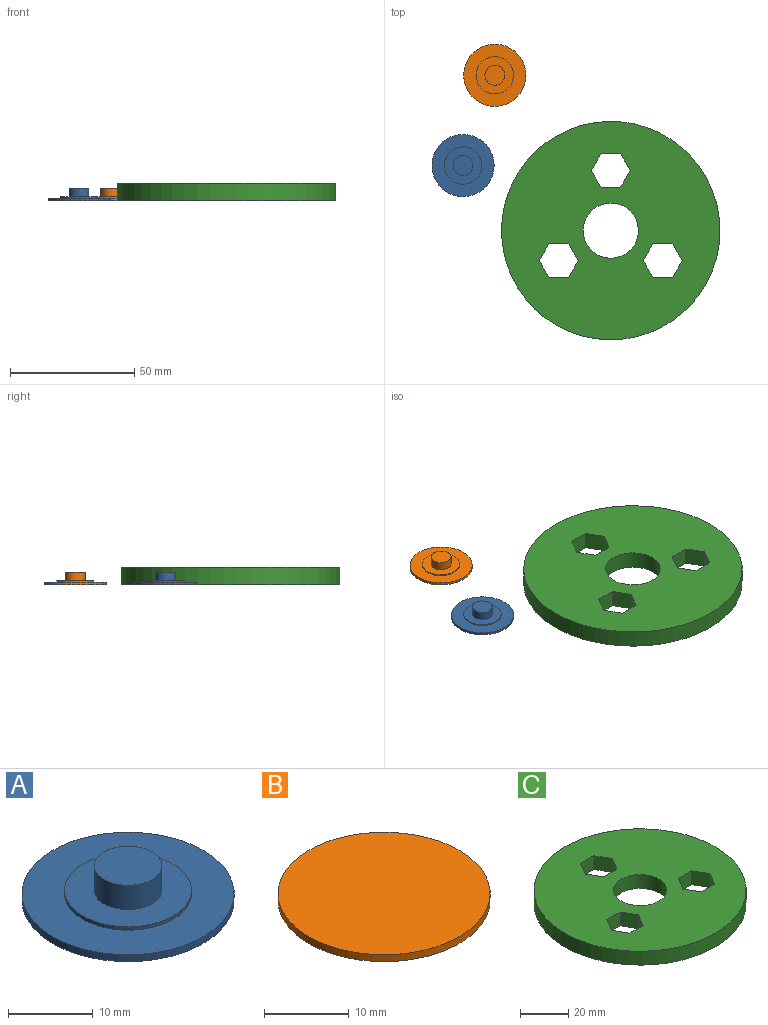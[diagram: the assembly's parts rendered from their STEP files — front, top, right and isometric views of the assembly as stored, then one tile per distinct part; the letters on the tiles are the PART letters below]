
ASSEMBLY  parts=3 mates=2
PART A: 124 faces, bbox 25x25x5 mm
  f0: plane 25x25mm, normal (0,0,-1), area 410mm2, adj f6,f7,f8,f9,f12,f20,f21,f22
  f1: cylinder r=4mm len=8mm, axis (0,0,1), area 88mm2, adj f2,f3
  f2: plane 8x8mm, normal (0,0,1), area 50.3mm2, adj f1
  f3: plane 15x15mm, normal (0,0,1), area 126.4mm2, adj f1,f4
  f4: cylinder r=7.5mm len=15mm, axis (0,0,1), area 23.6mm2, adj f3,f5
  f5: plane 25x25mm, normal (0,0,1), area 314.2mm2, adj f4,f6
  f6: cylinder r=12.5mm len=25mm, axis (0,0,1), area 78.5mm2, adj f0,f5
  f7: extruded ~0.28x0.25mm, area 0.1mm2, adj f0,f8,f12,f13
  f8: cylinder r=3.22mm len=6.45mm, axis (0,0,-1), area 4.7mm2, adj f0,f7,f9,f13
  f9: extruded ~0.29x0.25mm, area 0.1mm2, adj f0,f8,f12,f13
  f10: cylinder r=2.57mm len=5.14mm, axis (0,0,-1), area 4mm2, adj f13,f17
  f11: cylinder r=2.62mm len=5.24mm, axis (0,0,-1), area 4.1mm2, adj f13,f14
  f12: cylinder r=3.28mm len=6.56mm, axis (0,0,-1), area 4.8mm2, adj f0,f7,f9,f13
  f13: plane 13x6.64mm, normal (0,0,-1), area 24.1mm2, adj f7,f8,f9,f10,f11,f12
  f14: plane 5.24x5.24mm, normal (0,0,-1), area 9mm2, adj f11,f15
  f15: cylinder r=2mm len=3.99mm, axis (0,0,-1), area 3.1mm2, adj f14,f16
  f16: plane 3.99x3.99mm, normal (0,0,-1), area 12.5mm2, adj f15
  f17: plane 5.14x5.14mm, normal (0,0,-1), area 9.4mm2, adj f10,f18
  f18: cylinder r=1.9mm len=3.8mm, axis (0,0,-1), area 3mm2, adj f17,f19
  f19: plane 3.8x3.8mm, normal (0,0,-1), area 11.4mm2, adj f18
  f20: extruded ~0.25x0.21mm, area 0.1mm2, adj f0,f21,f35,f36
  f21: extruded ~0.27x0.25mm, area 0.1mm2, adj f0,f20,f22,f36
  f22: extruded ~0.31x0.25mm, area 0.1mm2, adj f0,f21,f23,f36
  f23: extruded ~0.31x0.25mm, area 0.1mm2, adj f0,f22,f24,f36
  f24: extruded ~0.56x0.25mm, area 0.2mm2, adj f0,f23,f25,f36
  f25: plane 0.34x0.25mm, normal (-1,0,0), area 0.1mm2, adj f0,f24,f26,f36
  f26: extruded ~0.27x0.25mm, area 0.1mm2, adj f0,f25,f27,f36
  f27: extruded ~0.27x0.25mm, area 0.1mm2, adj f0,f26,f28,f36
  f28: extruded ~0.25x0.22mm, area 0.1mm2, adj f0,f27,f29,f36
  f29: extruded ~0.26x0.25mm, area 0.1mm2, adj f0,f28,f30,f36
  f30: extruded ~0.33x0.25mm, area 0.1mm2, adj f0,f29,f31,f36
  f31: extruded ~0.28x0.25mm, area 0.1mm2, adj f0,f30,f32,f36
  f32: extruded ~0.56x0.25mm, area 0.2mm2, adj f0,f31,f33,f36
  f33: plane 0.35x0.25mm, normal (1,0,0), area 0.1mm2, adj f0,f32,f34,f36
  f34: extruded ~0.27x0.25mm, area 0.1mm2, adj f0,f33,f35,f36
  f35: extruded ~0.27x0.25mm, area 0.1mm2, adj f0,f20,f34,f36
  f36: plane 2.2x0.6mm, normal (0,0,-1), area 0.7mm2, adj f20,f21,f22,f23,f24,f25,f26,f27
  f37: plane 3.56x0.25mm, normal (-1,0,0), area 0.9mm2, adj f0,f38,f40,f41
  f38: plane 0.38x0.25mm, normal (0,1,0), area 0.1mm2, adj f0,f37,f39,f41
  f39: plane 3.56x0.25mm, normal (1,0,0), area 0.9mm2, adj f0,f38,f40,f41
  f40: plane 0.38x0.25mm, normal (0,-1,0), area 0.1mm2, adj f0,f37,f39,f41
  f41: plane 3.56x0.38mm, normal (0,0,-1), area 1.4mm2, adj f37,f38,f39,f40
  f42: plane 1.28x0.92mm, normal (0.81,0.58,0), area 0.4mm2, adj f0,f43,f53,f54
  f43: plane 0.43x0.25mm, normal (0,-1,0), area 0.1mm2, adj f0,f42,f44,f54
  f44: plane 1.02x0.71mm, normal (-0.82,-0.57,0), area 0.3mm2, adj f0,f43,f45,f54
  f45: plane 1.02x0.7mm, normal (0.82,-0.57,0), area 0.3mm2, adj f0,f44,f46,f54
  f46: plane 0.43x0.25mm, normal (0,-1,0), area 0.1mm2, adj f0,f45,f47,f54
  f47: plane 1.28x0.92mm, normal (-0.81,0.58,0), area 0.4mm2, adj f0,f46,f48,f54
  f48: plane 1.22x0.87mm, normal (-0.81,-0.58,0), area 0.4mm2, adj f0,f47,f49,f54
  f49: plane 0.43x0.25mm, normal (0,1,0), area 0.1mm2, adj f0,f48,f50,f54
  f50: plane 0.96x0.66mm, normal (0.82,0.57,0), area 0.3mm2, adj f0,f49,f51,f54
  f51: plane 0.96x0.66mm, normal (-0.82,0.57,0), area 0.3mm2, adj f0,f50,f52,f54
  f52: plane 0.43x0.25mm, normal (0,1,0), area 0.1mm2, adj f0,f51,f53,f54
  f53: plane 1.22x0.87mm, normal (0.81,-0.58,0), area 0.4mm2, adj f0,f42,f52,f54
  f54: plane 2.51x2.27mm, normal (0,0,-1), area 2mm2, adj f42,f43,f44,f45,f46,f47,f48,f49
  f55: extruded ~0.25x0.21mm, area 0.1mm2, adj f0,f56,f70,f71
  f56: extruded ~0.27x0.25mm, area 0.1mm2, adj f0,f55,f57,f71
  f57: extruded ~0.31x0.25mm, area 0.1mm2, adj f0,f56,f58,f71
  f58: extruded ~0.31x0.25mm, area 0.1mm2, adj f0,f57,f59,f71
  f59: extruded ~0.56x0.25mm, area 0.2mm2, adj f0,f58,f60,f71
  f60: plane 0.34x0.25mm, normal (-1,0,0), area 0.1mm2, adj f0,f59,f61,f71
  f61: extruded ~0.27x0.25mm, area 0.1mm2, adj f0,f60,f62,f71
  f62: extruded ~0.27x0.25mm, area 0.1mm2, adj f0,f61,f63,f71
  f63: extruded ~0.25x0.22mm, area 0.1mm2, adj f0,f62,f64,f71
  f64: extruded ~0.26x0.25mm, area 0.1mm2, adj f0,f63,f65,f71
  f65: extruded ~0.33x0.25mm, area 0.1mm2, adj f0,f64,f66,f71
  f66: extruded ~0.28x0.25mm, area 0.1mm2, adj f0,f65,f67,f71
  f67: extruded ~0.56x0.25mm, area 0.2mm2, adj f0,f66,f68,f71
  f68: plane 0.35x0.25mm, normal (1,0,0), area 0.1mm2, adj f0,f67,f69,f71
  f69: extruded ~0.27x0.25mm, area 0.1mm2, adj f0,f68,f70,f71
  f70: extruded ~0.27x0.25mm, area 0.1mm2, adj f0,f55,f69,f71
  f71: plane 2.2x0.6mm, normal (0,0,-1), area 0.7mm2, adj f55,f56,f57,f58,f59,f60,f61,f62
  f72: extruded ~0.43x0.25mm, area 0.1mm2, adj f0,f73,f90,f91
  f73: extruded ~0.38x0.25mm, area 0.1mm2, adj f0,f72,f74,f91
  f74: plane 0.34x0.25mm, normal (-1,0,0), area 0.1mm2, adj f0,f73,f75,f91
  f75: extruded ~0.8x0.25mm, area 0.2mm2, adj f0,f74,f76,f91
  f76: extruded ~0.6x0.25mm, area 0.2mm2, adj f0,f75,f77,f91
  f77: extruded ~0.67x0.25mm, area 0.2mm2, adj f0,f76,f78,f91
  f78: plane 1.73x0.25mm, normal (0,-1,0), area 0.4mm2, adj f0,f77,f79,f91
  f79: plane 0.25x0.24mm, normal (-1,0,0), area 0.1mm2, adj f0,f78,f80,f91
  f80: extruded ~0.82x0.27mm, area 0.2mm2, adj f0,f79,f81,f91
  f81: extruded ~0.75x0.31mm, area 0.2mm2, adj f0,f80,f82,f91
  f82: extruded ~0.8x0.36mm, area 0.2mm2, adj f0,f81,f83,f91
  f83: extruded ~0.96x0.3mm, area 0.3mm2, adj f0,f82,f84,f91
  f84: extruded ~0.94x0.32mm, area 0.3mm2, adj f0,f83,f90,f91
  f85: extruded ~0.46x0.25mm, area 0.1mm2, adj f86,f89,f91,f92
  f86: extruded ~0.55x0.25mm, area 0.1mm2, adj f85,f87,f91,f92
  f87: plane 1.31x0.25mm, normal (0,1,0), area 0.3mm2, adj f86,f88,f91,f92
  f88: extruded ~0.54x0.25mm, area 0.1mm2, adj f87,f89,f91,f92
  f89: extruded ~0.48x0.25mm, area 0.1mm2, adj f85,f88,f91,f92
  f90: extruded ~0.88x0.34mm, area 0.2mm2, adj f0,f72,f84,f91
  f91: plane 2.6x2.12mm, normal (0,0,-1), area 2.5mm2, adj f72,f73,f74,f75,f76,f77,f78,f79
  f92: plane 1.31x0.74mm, normal (0,0,-1), area 0.8mm2, adj f85,f86,f87,f88,f89
  f93: plane 0.4x0.25mm, normal (0,-1,0), area 0.1mm2, adj f0,f94,f105,f106
  f94: plane 3.36x1.32mm, normal (-0.93,0.36,0), area 0.9mm2, adj f0,f93,f95,f106
  f95: plane 0.33x0.25mm, normal (0,1,0), area 0.1mm2, adj f0,f94,f96,f106
  f96: plane 3.36x1.32mm, normal (0.93,0.37,0), area 0.9mm2, adj f0,f95,f97,f106
  f97: plane 0.39x0.25mm, normal (0,-1,0), area 0.1mm2, adj f0,f96,f98,f106
  f98: plane 1.06x0.41mm, normal (-0.93,-0.36,0), area 0.3mm2, adj f0,f97,f99,f106
  f99: plane 1.34x0.25mm, normal (0,-1,0), area 0.3mm2, adj f0,f98,f105,f106
  f100: plane 1.08x0.25mm, normal (0,1,0), area 0.3mm2, adj f101,f104,f106,f107
  f101: plane 1.04x0.39mm, normal (-0.94,-0.35,0), area 0.3mm2, adj f100,f102,f106,f107
  f102: extruded ~0.48x0.25mm, area 0.1mm2, adj f101,f103,f106,f107
  f103: extruded ~0.48x0.25mm, area 0.1mm2, adj f102,f104,f106,f107
  f104: plane 1.04x0.39mm, normal (0.94,-0.35,0), area 0.3mm2, adj f100,f103,f106,f107
  f105: plane 1.06x0.42mm, normal (0.93,-0.36,0), area 0.3mm2, adj f0,f93,f99,f106
  f106: plane 3.36x2.96mm, normal (0,0,-1), area 2.9mm2, adj f93,f94,f95,f96,f97,f98,f99,f100
  f107: plane 1.52x1.08mm, normal (0,0,-1), area 0.8mm2, adj f100,f101,f102,f103,f104
  f108: plane 0.35x0.25mm, normal (1,0,0), area 0.1mm2, adj f0,f109,f114,f115
  f109: plane 2.2x0.97mm, normal (-0.4,-0.92,0), area 0.6mm2, adj f0,f108,f110,f115
  f110: plane 0.25x0.22mm, normal (-1,0,0), area 0.1mm2, adj f0,f109,f111,f115
  f111: plane 2.2x1.1mm, normal (-0.45,0.89,0), area 0.6mm2, adj f0,f110,f112,f115
  f112: plane 0.34x0.25mm, normal (1,0,0), area 0.1mm2, adj f0,f111,f113,f115
  f113: plane 1.79x0.85mm, normal (0.43,-0.9,0), area 0.5mm2, adj f0,f112,f114,f115
  f114: plane 1.79x0.75mm, normal (0.38,0.92,0), area 0.5mm2, adj f0,f108,f113,f115
  f115: plane 2.28x2.2mm, normal (0,0,-1), area 1.3mm2, adj f108,f109,f110,f111,f112,f113,f114
  f116: plane 0.35x0.25mm, normal (-1,0,0), area 0.1mm2, adj f0,f117,f122,f123
  f117: plane 1.79x0.75mm, normal (-0.39,0.92,0), area 0.5mm2, adj f0,f116,f118,f123
  f118: plane 1.79x0.85mm, normal (-0.43,-0.9,0), area 0.5mm2, adj f0,f117,f119,f123
  f119: plane 0.34x0.25mm, normal (-1,0,0), area 0.1mm2, adj f0,f118,f120,f123
  f120: plane 2.2x1.1mm, normal (0.45,0.89,0), area 0.6mm2, adj f0,f119,f121,f123
  f121: plane 0.25x0.22mm, normal (1,0,0), area 0.1mm2, adj f0,f120,f122,f123
  f122: plane 2.2x0.97mm, normal (0.4,-0.92,0), area 0.6mm2, adj f0,f116,f121,f123
  f123: plane 2.28x2.2mm, normal (0,0,-1), area 1.3mm2, adj f116,f117,f118,f119,f120,f121,f122
PART B: 7 faces, bbox 25x25x5 mm
  f0: cylinder r=4mm len=8mm, axis (0,0,-1), area 88mm2, adj f1,f2
  f1: plane 8x8mm, normal (0,0,-1), area 50.3mm2, adj f0
  f2: plane 15x15mm, normal (0,0,-1), area 126.4mm2, adj f0,f3
  f3: cylinder r=7.5mm len=15mm, axis (0,0,-1), area 23.6mm2, adj f2,f4
  f4: plane 25x25mm, normal (0,0,-1), area 314.2mm2, adj f3,f6
  f5: plane 25x25mm, normal (0,0,1), area 490.9mm2, adj f6
  f6: cylinder r=12.5mm len=25mm, axis (0,0,-1), area 78.5mm2, adj f4,f5
PART C: 23 faces, bbox 87.8x87.8x7 mm
  f0: plane 87.84x87.84mm, normal (0,0,-1), area 5192.2mm2, adj f2,f3,f4,f5,f6,f7,f8,f9
  f1: plane 87.84x87.84mm, normal (0,0,1), area 5192.2mm2, adj f2,f3,f4,f5,f6,f7,f8,f9
  f2: cylinder r=11.1mm len=22.2mm, axis (0,0,-1), area 488.2mm2, adj f0,f1
  f3: plane 7.85x7mm, normal (0,1,0), area 55mm2, adj f0,f1,f4,f8
  f4: plane 7x6.8mm, normal (-0.87,0.5,0), area 55mm2, adj f0,f1,f3,f5
  f5: plane 7x6.8mm, normal (-0.87,-0.5,0), area 55mm2, adj f0,f1,f4,f6
  f6: plane 7.85x7mm, normal (0,-1,0), area 55mm2, adj f0,f1,f5,f7
  f7: plane 7x6.8mm, normal (0.87,-0.5,0), area 55mm2, adj f0,f1,f6,f8
  f8: plane 7x6.8mm, normal (0.87,0.5,0), area 55mm2, adj f0,f1,f3,f7
  f9: plane 7x6.8mm, normal (0.87,-0.5,0), area 55mm2, adj f0,f1,f10,f14
  f10: plane 7x6.8mm, normal (0.87,0.5,0), area 55mm2, adj f0,f1,f9,f11
  f11: plane 7.85x7mm, normal (0,1,0), area 55mm2, adj f0,f1,f10,f12
  f12: plane 7x6.8mm, normal (-0.87,0.5,0), area 55mm2, adj f0,f1,f11,f13
  f13: plane 7x6.8mm, normal (-0.87,-0.5,0), area 55mm2, adj f0,f1,f12,f14
  f14: plane 7.85x7mm, normal (0,-1,0), area 55mm2, adj f0,f1,f9,f13
  f15: plane 7.85x7mm, normal (0,-1,0), area 55mm2, adj f0,f1,f16,f20
  f16: plane 7x6.8mm, normal (0.87,-0.5,0), area 55mm2, adj f0,f1,f15,f17
  f17: plane 7x6.8mm, normal (0.87,0.5,0), area 55mm2, adj f0,f1,f16,f18
  f18: plane 7.25x7mm, normal (0,1,0), area 50.7mm2, adj f0,f1,f17,f21
  f19: plane 7x5.44mm, normal (-0.87,0.5,0), area 44mm2, adj f0,f1,f20,f21
  f20: plane 7x6.8mm, normal (-0.87,-0.5,0), area 55mm2, adj f0,f1,f15,f19
  f21: extruded ~7x1.39mm, area 13.6mm2, adj f0,f1,f18,f19
  f22: cylinder r=43.92mm len=87.84mm, axis (0,0,1), area 1931.6mm2, adj f0,f1
PLACE A t=(-59.42,26.17,7.75)mm
PLACE B rot(axis=(1,0,0),180deg) t=(-46.64,62.47,7.75)mm
PLACE C t=(0,0,6.25)mm
MATE planar A.f8 <-> C.f0  axis (0,0,-1) through (-62.65,19.24,2.75)mm
MATE planar B.f0 <-> C.f0  axis (0,0,-1) through (-46.64,62.47,2.75)mm
